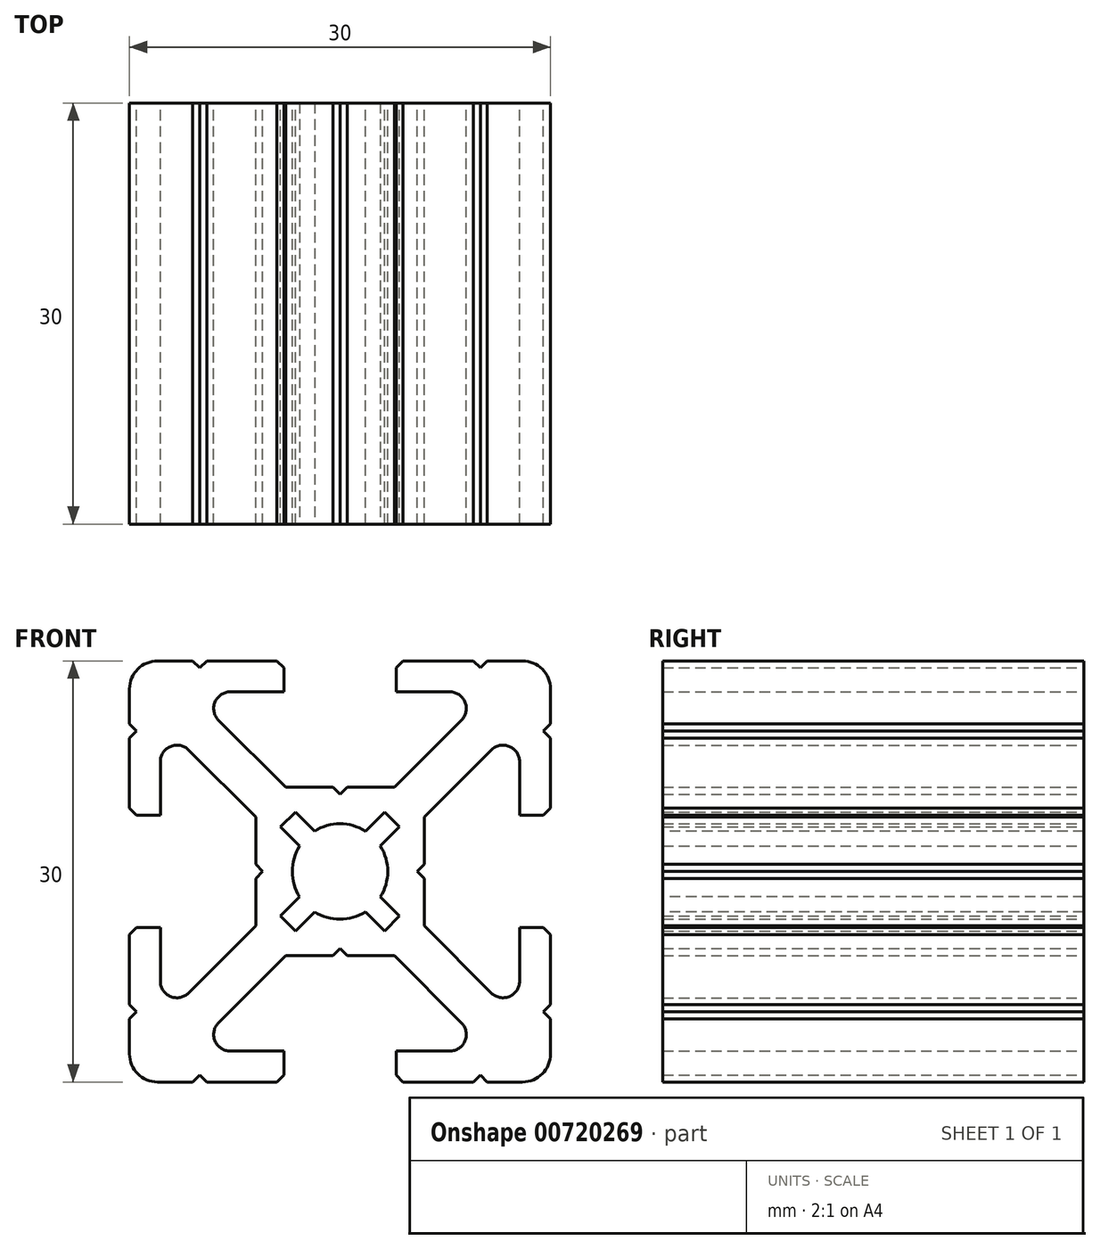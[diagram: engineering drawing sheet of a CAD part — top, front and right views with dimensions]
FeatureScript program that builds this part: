
annotation { "Feature Type Name" : "Feature", "Feature Type Description" : "" }
export const myFeature = defineFeature(function(context is Context, id is Id, definition is map)
    precondition{}
    {
        {
            var Q0;
            Q0=qCreatedBy(makeId("Front.planeOp"),FACE);
            var sketch = newSketch(context, id + "F0", { "sketchPlane" : qUnion([Q0])});
            skLineSegment(sketch, "E0", {"start": v(-2.88, -1.81) * mm, "end": v(-4.24, -3.18) * mm});
            skLineSegment(sketch, "E1", {"start": v(-4.24, -3.18) * mm, "end": v(-3.18, -4.24) * mm});
            skLineSegment(sketch, "E2", {"start": v(-3.18, -4.24) * mm, "end": v(-1.81, -2.88) * mm});
            skLineSegment(sketch, "E3", {"start": v(-1.81, -2.88) * mm, "end": v(-1.81, -2.88) * mm});
            skArc(sketch, "E4", {"start": v(-1.81, -2.88) * mm, "mid": v(0, -3.4) * mm, "end": v(1.81, -2.88) * mm});
            skLineSegment(sketch, "E5", {"start": v(1.81, -2.88) * mm, "end": v(1.81, -2.88) * mm});
            skLineSegment(sketch, "E6", {"start": v(1.81, -2.88) * mm, "end": v(3.18, -4.24) * mm});
            skLineSegment(sketch, "E7", {"start": v(3.18, -4.24) * mm, "end": v(4.24, -3.18) * mm});
            skLineSegment(sketch, "E8", {"start": v(4.24, -3.18) * mm, "end": v(2.88, -1.81) * mm});
            skLineSegment(sketch, "E9", {"start": v(2.88, -1.81) * mm, "end": v(2.88, -1.81) * mm});
            skArc(sketch, "E10", {"start": v(2.88, -1.81) * mm, "mid": v(3.4, 0) * mm, "end": v(2.88, 1.81) * mm});
            skLineSegment(sketch, "E11", {"start": v(2.88, 1.81) * mm, "end": v(2.88, 1.81) * mm});
            skLineSegment(sketch, "E12", {"start": v(2.88, 1.81) * mm, "end": v(4.24, 3.18) * mm});
            skLineSegment(sketch, "E13", {"start": v(4.24, 3.18) * mm, "end": v(3.18, 4.24) * mm});
            skLineSegment(sketch, "E14", {"start": v(3.18, 4.24) * mm, "end": v(1.81, 2.88) * mm});
            skLineSegment(sketch, "E15", {"start": v(1.81, 2.88) * mm, "end": v(1.81, 2.88) * mm});
            skArc(sketch, "E16", {"start": v(1.81, 2.88) * mm, "mid": v(0, 3.4) * mm, "end": v(-1.81, 2.88) * mm});
            skLineSegment(sketch, "E17", {"start": v(-1.81, 2.88) * mm, "end": v(-1.81, 2.88) * mm});
            skLineSegment(sketch, "E18", {"start": v(-1.81, 2.88) * mm, "end": v(-3.18, 4.24) * mm});
            skLineSegment(sketch, "E19", {"start": v(-3.18, 4.24) * mm, "end": v(-4.24, 3.18) * mm});
            skLineSegment(sketch, "E20", {"start": v(-4.24, 3.18) * mm, "end": v(-2.88, 1.81) * mm});
            skLineSegment(sketch, "E21", {"start": v(-2.88, 1.81) * mm, "end": v(-2.88, 1.81) * mm});
            skArc(sketch, "E22", {"start": v(-2.88, 1.81) * mm, "mid": v(-3.4, 0) * mm, "end": v(-2.88, -1.81) * mm});
            skArc(sketch, "E23", {"start": v(-10.77, 8.65) * mm, "mid": v(-11.38, 8.98) * mm, "end": v(-12.07, 8.9) * mm});
            skArc(sketch, "E24", {"start": v(-12.07, 8.9) * mm, "mid": v(-12.6, 8.47) * mm, "end": v(-12.8, 7.81) * mm});
            skLineSegment(sketch, "E25", {"start": v(-12.8, 7.81) * mm, "end": v(-12.8, 4) * mm});
            skLineSegment(sketch, "E26", {"start": v(-12.8, 4) * mm, "end": v(-14.5, 4) * mm});
            skLineSegment(sketch, "E27", {"start": v(-14.5, 4) * mm, "end": v(-15, 4.5) * mm});
            skLineSegment(sketch, "E28", {"start": v(-15, 4.5) * mm, "end": v(-15, 9.5) * mm});
            skLineSegment(sketch, "E29", {"start": v(-15, 9.5) * mm, "end": v(-14.5, 10) * mm});
            skLineSegment(sketch, "E30", {"start": v(-14.5, 10) * mm, "end": v(-15, 10.5) * mm});
            skLineSegment(sketch, "E31", {"start": v(-15, 10.5) * mm, "end": v(-15, 13) * mm});
            skLineSegment(sketch, "E32", {"start": v(-15, 13) * mm, "end": v(-15, 13) * mm});
            skArc(sketch, "E33", {"start": v(-13, 15) * mm, "mid": v(-14.41, 14.41) * mm, "end": v(-15, 13) * mm});
            skLineSegment(sketch, "E34", {"start": v(-13, 15) * mm, "end": v(-13, 15) * mm});
            skLineSegment(sketch, "E35", {"start": v(-13, 15) * mm, "end": v(-10.5, 15) * mm});
            skLineSegment(sketch, "E36", {"start": v(-10.5, 15) * mm, "end": v(-10, 14.5) * mm});
            skLineSegment(sketch, "E37", {"start": v(-10, 14.5) * mm, "end": v(-9.5, 15) * mm});
            skLineSegment(sketch, "E38", {"start": v(-9.5, 15) * mm, "end": v(-4.5, 15) * mm});
            skLineSegment(sketch, "E39", {"start": v(-4.5, 15) * mm, "end": v(-4, 14.5) * mm});
            skLineSegment(sketch, "E40", {"start": v(-4, 14.5) * mm, "end": v(-4, 12.8) * mm});
            skLineSegment(sketch, "E41", {"start": v(-4, 12.8) * mm, "end": v(-7.81, 12.8) * mm});
            skArc(sketch, "E42", {"start": v(-7.81, 12.8) * mm, "mid": v(-8.47, 12.6) * mm, "end": v(-8.9, 12.07) * mm});
            skArc(sketch, "E43", {"start": v(-8.9, 12.07) * mm, "mid": v(-8.98, 11.38) * mm, "end": v(-8.65, 10.77) * mm});
            skLineSegment(sketch, "E44", {"start": v(-8.65, 10.77) * mm, "end": v(-3.88, 6) * mm});
            skLineSegment(sketch, "E45", {"start": v(-3.88, 6) * mm, "end": v(-0.5, 6) * mm});
            skLineSegment(sketch, "E46", {"start": v(-0.5, 6) * mm, "end": v(0, 5.5) * mm});
            skLineSegment(sketch, "E47", {"start": v(0, 5.5) * mm, "end": v(0.5, 6) * mm});
            skLineSegment(sketch, "E48", {"start": v(0.5, 6) * mm, "end": v(3.88, 6) * mm});
            skLineSegment(sketch, "E49", {"start": v(3.88, 6) * mm, "end": v(8.65, 10.77) * mm});
            skArc(sketch, "E50", {"start": v(8.65, 10.77) * mm, "mid": v(8.98, 11.38) * mm, "end": v(8.9, 12.07) * mm});
            skArc(sketch, "E51", {"start": v(8.9, 12.07) * mm, "mid": v(8.47, 12.6) * mm, "end": v(7.81, 12.8) * mm});
            skLineSegment(sketch, "E52", {"start": v(7.81, 12.8) * mm, "end": v(4, 12.8) * mm});
            skLineSegment(sketch, "E53", {"start": v(4, 12.8) * mm, "end": v(4, 14.5) * mm});
            skLineSegment(sketch, "E54", {"start": v(4, 14.5) * mm, "end": v(4.5, 15) * mm});
            skLineSegment(sketch, "E55", {"start": v(4.5, 15) * mm, "end": v(9.5, 15) * mm});
            skLineSegment(sketch, "E56", {"start": v(9.5, 15) * mm, "end": v(10, 14.5) * mm});
            skLineSegment(sketch, "E57", {"start": v(10, 14.5) * mm, "end": v(10.5, 15) * mm});
            skLineSegment(sketch, "E58", {"start": v(10.5, 15) * mm, "end": v(13, 15) * mm});
            skLineSegment(sketch, "E59", {"start": v(13, 15) * mm, "end": v(13, 15) * mm});
            skArc(sketch, "E60", {"start": v(15, 13) * mm, "mid": v(14.41, 14.41) * mm, "end": v(13, 15) * mm});
            skLineSegment(sketch, "E61", {"start": v(15, 13) * mm, "end": v(15, 13) * mm});
            skLineSegment(sketch, "E62", {"start": v(15, 13) * mm, "end": v(15, 10.5) * mm});
            skLineSegment(sketch, "E63", {"start": v(15, 10.5) * mm, "end": v(14.5, 10) * mm});
            skLineSegment(sketch, "E64", {"start": v(14.5, 10) * mm, "end": v(15, 9.5) * mm});
            skLineSegment(sketch, "E65", {"start": v(15, 9.5) * mm, "end": v(15, 4.5) * mm});
            skLineSegment(sketch, "E66", {"start": v(15, 4.5) * mm, "end": v(14.5, 4) * mm});
            skLineSegment(sketch, "E67", {"start": v(14.5, 4) * mm, "end": v(12.8, 4) * mm});
            skLineSegment(sketch, "E68", {"start": v(12.8, 4) * mm, "end": v(12.8, 7.81) * mm});
            skArc(sketch, "E69", {"start": v(12.8, 7.81) * mm, "mid": v(12.6, 8.47) * mm, "end": v(12.07, 8.9) * mm});
            skArc(sketch, "E70", {"start": v(12.07, 8.9) * mm, "mid": v(11.38, 8.98) * mm, "end": v(10.77, 8.65) * mm});
            skLineSegment(sketch, "E71", {"start": v(10.77, 8.65) * mm, "end": v(10.77, 8.65) * mm});
            skLineSegment(sketch, "E72", {"start": v(10.77, 8.65) * mm, "end": v(6, 3.88) * mm});
            skLineSegment(sketch, "E73", {"start": v(6, 3.88) * mm, "end": v(6, 0.5) * mm});
            skLineSegment(sketch, "E74", {"start": v(6, 0.5) * mm, "end": v(5.5, 0) * mm});
            skLineSegment(sketch, "E75", {"start": v(5.5, 0) * mm, "end": v(6, -0.5) * mm});
            skLineSegment(sketch, "E76", {"start": v(6, -0.5) * mm, "end": v(6, -3.88) * mm});
            skLineSegment(sketch, "E77", {"start": v(6, -3.88) * mm, "end": v(10.77, -8.65) * mm});
            skLineSegment(sketch, "E78", {"start": v(10.77, -8.65) * mm, "end": v(10.77, -8.65) * mm});
            skArc(sketch, "E79", {"start": v(10.77, -8.65) * mm, "mid": v(11.38, -8.98) * mm, "end": v(12.07, -8.9) * mm});
            skArc(sketch, "E80", {"start": v(12.07, -8.9) * mm, "mid": v(12.6, -8.47) * mm, "end": v(12.8, -7.81) * mm});
            skLineSegment(sketch, "E81", {"start": v(12.8, -7.81) * mm, "end": v(12.8, -4) * mm});
            skLineSegment(sketch, "E82", {"start": v(12.8, -4) * mm, "end": v(14.5, -4) * mm});
            skLineSegment(sketch, "E83", {"start": v(14.5, -4) * mm, "end": v(15, -4.5) * mm});
            skLineSegment(sketch, "E84", {"start": v(15, -4.5) * mm, "end": v(15, -9.5) * mm});
            skLineSegment(sketch, "E85", {"start": v(15, -9.5) * mm, "end": v(14.5, -10) * mm});
            skLineSegment(sketch, "E86", {"start": v(14.5, -10) * mm, "end": v(15, -10.5) * mm});
            skLineSegment(sketch, "E87", {"start": v(15, -10.5) * mm, "end": v(15, -13) * mm});
            skLineSegment(sketch, "E88", {"start": v(15, -13) * mm, "end": v(15, -13) * mm});
            skArc(sketch, "E89", {"start": v(13, -15) * mm, "mid": v(14.41, -14.41) * mm, "end": v(15, -13) * mm});
            skLineSegment(sketch, "E90", {"start": v(13, -15) * mm, "end": v(13, -15) * mm});
            skLineSegment(sketch, "E91", {"start": v(13, -15) * mm, "end": v(10.5, -15) * mm});
            skLineSegment(sketch, "E92", {"start": v(10.5, -15) * mm, "end": v(10, -14.5) * mm});
            skLineSegment(sketch, "E93", {"start": v(10, -14.5) * mm, "end": v(9.5, -15) * mm});
            skLineSegment(sketch, "E94", {"start": v(9.5, -15) * mm, "end": v(4.5, -15) * mm});
            skLineSegment(sketch, "E95", {"start": v(4.5, -15) * mm, "end": v(4, -14.5) * mm});
            skLineSegment(sketch, "E96", {"start": v(4, -14.5) * mm, "end": v(4, -12.8) * mm});
            skLineSegment(sketch, "E97", {"start": v(4, -12.8) * mm, "end": v(7.81, -12.8) * mm});
            skArc(sketch, "E98", {"start": v(7.81, -12.8) * mm, "mid": v(8.47, -12.6) * mm, "end": v(8.9, -12.07) * mm});
            skArc(sketch, "E99", {"start": v(8.9, -12.07) * mm, "mid": v(8.98, -11.38) * mm, "end": v(8.65, -10.77) * mm});
            skLineSegment(sketch, "E100", {"start": v(8.65, -10.77) * mm, "end": v(3.88, -6) * mm});
            skLineSegment(sketch, "E101", {"start": v(3.88, -6) * mm, "end": v(0.5, -6) * mm});
            skLineSegment(sketch, "E102", {"start": v(0.5, -6) * mm, "end": v(0, -5.5) * mm});
            skLineSegment(sketch, "E103", {"start": v(0, -5.5) * mm, "end": v(-0.5, -6) * mm});
            skLineSegment(sketch, "E104", {"start": v(-0.5, -6) * mm, "end": v(-3.88, -6) * mm});
            skLineSegment(sketch, "E105", {"start": v(-3.88, -6) * mm, "end": v(-8.65, -10.77) * mm});
            skArc(sketch, "E106", {"start": v(-8.65, -10.77) * mm, "mid": v(-8.98, -11.38) * mm, "end": v(-8.9, -12.07) * mm});
            skArc(sketch, "E107", {"start": v(-8.9, -12.07) * mm, "mid": v(-8.47, -12.6) * mm, "end": v(-7.81, -12.8) * mm});
            skLineSegment(sketch, "E108", {"start": v(-7.81, -12.8) * mm, "end": v(-4, -12.8) * mm});
            skLineSegment(sketch, "E109", {"start": v(-4, -12.8) * mm, "end": v(-4, -14.5) * mm});
            skLineSegment(sketch, "E110", {"start": v(-4, -14.5) * mm, "end": v(-4.5, -15) * mm});
            skLineSegment(sketch, "E111", {"start": v(-4.5, -15) * mm, "end": v(-9.5, -15) * mm});
            skLineSegment(sketch, "E112", {"start": v(-9.5, -15) * mm, "end": v(-10, -14.5) * mm});
            skLineSegment(sketch, "E113", {"start": v(-10, -14.5) * mm, "end": v(-10.5, -15) * mm});
            skLineSegment(sketch, "E114", {"start": v(-10.5, -15) * mm, "end": v(-13, -15) * mm});
            skLineSegment(sketch, "E115", {"start": v(-13, -15) * mm, "end": v(-13, -15) * mm});
            skArc(sketch, "E116", {"start": v(-15, -13) * mm, "mid": v(-14.41, -14.41) * mm, "end": v(-13, -15) * mm});
            skLineSegment(sketch, "E117", {"start": v(-15, -13) * mm, "end": v(-15, -13) * mm});
            skLineSegment(sketch, "E118", {"start": v(-15, -13) * mm, "end": v(-15, -10.5) * mm});
            skLineSegment(sketch, "E119", {"start": v(-15, -10.5) * mm, "end": v(-14.5, -10) * mm});
            skLineSegment(sketch, "E120", {"start": v(-14.5, -10) * mm, "end": v(-15, -9.5) * mm});
            skLineSegment(sketch, "E121", {"start": v(-15, -9.5) * mm, "end": v(-15, -4.5) * mm});
            skLineSegment(sketch, "E122", {"start": v(-15, -4.5) * mm, "end": v(-14.5, -4) * mm});
            skLineSegment(sketch, "E123", {"start": v(-14.5, -4) * mm, "end": v(-12.8, -4) * mm});
            skLineSegment(sketch, "E124", {"start": v(-12.8, -4) * mm, "end": v(-12.8, -7.81) * mm});
            skArc(sketch, "E125", {"start": v(-12.8, -7.81) * mm, "mid": v(-12.6, -8.47) * mm, "end": v(-12.07, -8.9) * mm});
            skArc(sketch, "E126", {"start": v(-12.07, -8.9) * mm, "mid": v(-11.38, -8.98) * mm, "end": v(-10.77, -8.65) * mm});
            skLineSegment(sketch, "E127", {"start": v(-10.77, -8.65) * mm, "end": v(-10.77, -8.65) * mm});
            skLineSegment(sketch, "E128", {"start": v(-10.77, -8.65) * mm, "end": v(-6, -3.88) * mm});
            skLineSegment(sketch, "E129", {"start": v(-6, -3.88) * mm, "end": v(-6, -0.5) * mm});
            skLineSegment(sketch, "E130", {"start": v(-6, -0.5) * mm, "end": v(-5.5, 0) * mm});
            skLineSegment(sketch, "E131", {"start": v(-5.5, 0) * mm, "end": v(-6, 0.5) * mm});
            skLineSegment(sketch, "E132", {"start": v(-6, 0.5) * mm, "end": v(-6, 3.88) * mm});
            skLineSegment(sketch, "E133", {"start": v(-6, 3.88) * mm, "end": v(-10.77, 8.65) * mm});
            skSolve(sketch);
        }
        {
            var Q0;
            Q0=makeQuery(id+"F0.imprint","IMPRINT",FACE,{"disambiguationData":[TD([[makeQuery(id+"F0.imprint","IMPRINT",EDGE,{"derivedFrom":sQuery(id+"F0.wireOp",EDGE,"E0")}),-1.0]])]});
            extrude(context, id + "F1", {"entities" : qUnion([Q0]), "depth" : 30 * mm, "offsetDistance" : 25 * mm});
        }
    });
